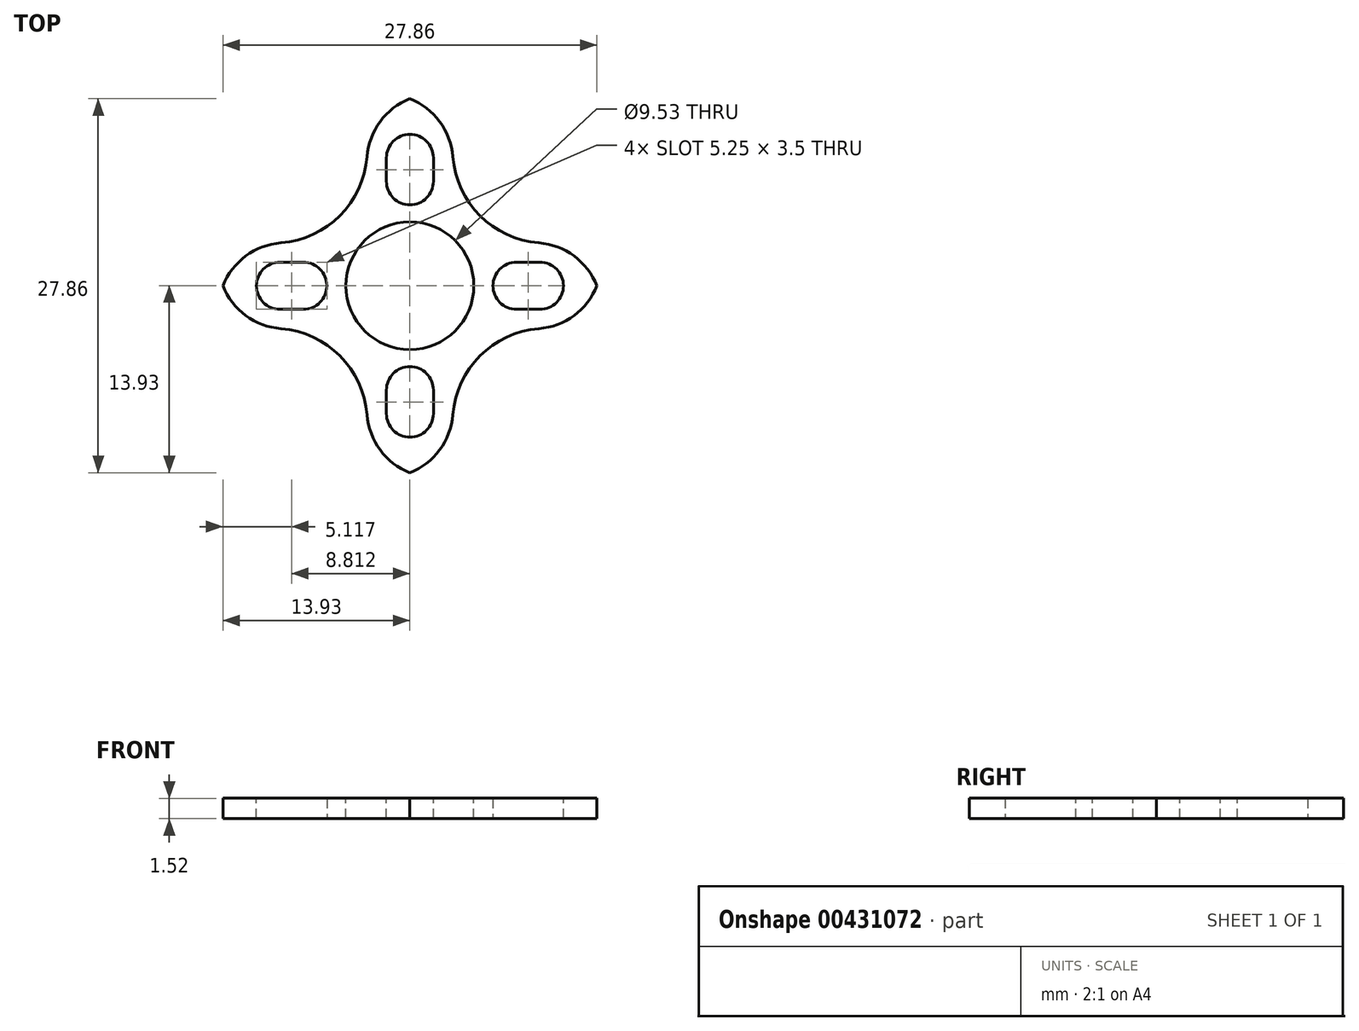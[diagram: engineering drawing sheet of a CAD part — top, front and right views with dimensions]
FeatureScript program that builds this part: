
annotation { "Feature Type Name" : "Feature", "Feature Type Description" : "" }
export const myFeature = defineFeature(function(context is Context, id is Id, definition is map)
    precondition{}
    {
        {
            var Q0;
            Q0=qCreatedBy(makeId("Top.planeOp"),FACE);
            var sketch = newSketch(context, id + "F0", { "sketchPlane" : qUnion([Q0])});
            skCircle(sketch, "E0", {"center": v(0, 9.52) * mm, "radius": 1.75 * mm});
            skCircle(sketch, "E1", {"center": v(0, -9.52) * mm, "radius": 1.75 * mm});
            skCircle(sketch, "E2", {"center": v(-7.94, 0) * mm, "radius": 1.75 * mm});
            skCircle(sketch, "E3", {"center": v(7.94, 0) * mm, "radius": 1.75 * mm});
            skLineSegment(sketch, "E4", {"start": v(-7.94, 0) * mm, "end": v(0, 0) * mm});
            skLineSegment(sketch, "E5", {"start": v(0, 0) * mm, "end": v(7.94, 0) * mm});
            skLineSegment(sketch, "E6", {"start": v(0, 9.53) * mm, "end": v(0, 0) * mm});
            skLineSegment(sketch, "E7", {"start": v(0, -9.53) * mm, "end": v(0, 0) * mm});
            skLineSegment(sketch, "E8", {"start": v(3.18, 14.29) * mm, "end": v(3.18, 3.18) * mm});
            skLineSegment(sketch, "E9", {"start": v(3.17, 3.18) * mm, "end": v(14.29, 3.18) * mm});
            skLineSegment(sketch, "E10", {"start": v(14.29, 3.18) * mm, "end": v(14.29, -3.17) * mm});
            skLineSegment(sketch, "E11", {"start": v(14.29, -3.18) * mm, "end": v(3.17, -3.18) * mm});
            skLineSegment(sketch, "E12", {"start": v(3.18, -3.18) * mm, "end": v(3.18, -14.29) * mm});
            skLineSegment(sketch, "E13", {"start": v(3.17, -14.29) * mm, "end": v(-3.18, -14.29) * mm});
            skLineSegment(sketch, "E14", {"start": v(-3.18, -14.29) * mm, "end": v(-3.18, -3.18) * mm});
            skLineSegment(sketch, "E15", {"start": v(-3.17, -3.18) * mm, "end": v(-14.29, -3.18) * mm});
            skLineSegment(sketch, "E16", {"start": v(-14.29, -3.17) * mm, "end": v(-14.29, 3.18) * mm});
            skLineSegment(sketch, "E17", {"start": v(-14.29, 3.18) * mm, "end": v(-3.18, 3.18) * mm});
            skLineSegment(sketch, "E18", {"start": v(-3.18, 3.18) * mm, "end": v(-3.18, 14.29) * mm});
            skLineSegment(sketch, "E19", {"start": v(-3.18, 14.29) * mm, "end": v(3.17, 14.29) * mm});
            skLineSegment(sketch, "E20", {"start": v(0, -9.52) * mm, "end": v(0, -14.29) * mm, "construction": true});
            skLineSegment(sketch, "E21", {"start": v(7.94, 0) * mm, "end": v(14.29, 0) * mm, "construction": true});
            skSolve(sketch);
        }
        {
            var Q0;
            Q0 = qSketchRegion(id + "F0", true);
            extrude(context, id + "F1", {"entities" : qUnion([Q0]), "depth" : 1.52 * mm});
        }
        {
            var Q0;
            Q0=makeQuery(id+"F1.opExtrude","SWEPT_EDGE",EDGE,{"disambiguationData":[OSD([sQuery(id+"F0.wireOp",EDGE,"E11"),sQuery(id+"F0.wireOp",EDGE,"E12")])]});
            var Q1;
            Q1=makeQuery(id+"F1.opExtrude","SWEPT_EDGE",EDGE,{"disambiguationData":[OSD([sQuery(id+"F0.wireOp",EDGE,"E17"),sQuery(id+"F0.wireOp",EDGE,"E18")])]});
            var Q2;
            Q2=makeQuery(id+"F1.opExtrude","SWEPT_EDGE",EDGE,{"disambiguationData":[OSD([sQuery(id+"F0.wireOp",EDGE,"E8"),sQuery(id+"F0.wireOp",EDGE,"E9")])]});
            var Q3;
            Q3=makeQuery(id+"F1.opExtrude","SWEPT_EDGE",EDGE,{"disambiguationData":[OSD([sQuery(id+"F0.wireOp",EDGE,"E14"),sQuery(id+"F0.wireOp",EDGE,"E15")])]});
            fillet(context, id + "F2", {"entities" : qUnion([Q0, Q1, Q2, Q3]), "radius" : 7 * mm, "tangentPropagation" : true, "allowEdgeOverflow" : false});
        }
        {
            var Q0;
            Q0=makeQuery(id+"F1.opExtrude","SWEPT_EDGE",EDGE,{"disambiguationData":[OSD([sQuery(id+"F0.wireOp",EDGE,"E8"),sQuery(id+"F0.wireOp",EDGE,"E19")])]});
            var Q1;
            Q1=makeQuery(id+"F1.opExtrude","SWEPT_EDGE",EDGE,{"disambiguationData":[OSD([sQuery(id+"F0.wireOp",EDGE,"E18"),sQuery(id+"F0.wireOp",EDGE,"E19")])]});
            var Q2;
            Q2=makeQuery(id+"F1.opExtrude","SWEPT_EDGE",EDGE,{"disambiguationData":[OSD([sQuery(id+"F0.wireOp",EDGE,"E15"),sQuery(id+"F0.wireOp",EDGE,"E16")])]});
            var Q3;
            Q3=makeQuery(id+"F1.opExtrude","SWEPT_EDGE",EDGE,{"disambiguationData":[OSD([sQuery(id+"F0.wireOp",EDGE,"E16"),sQuery(id+"F0.wireOp",EDGE,"E17")])]});
            var Q4;
            Q4=makeQuery(id+"F1.opExtrude","SWEPT_EDGE",EDGE,{"disambiguationData":[OSD([sQuery(id+"F0.wireOp",EDGE,"E13"),sQuery(id+"F0.wireOp",EDGE,"E14")])]});
            var Q5;
            Q5=makeQuery(id+"F1.opExtrude","SWEPT_EDGE",EDGE,{"disambiguationData":[OSD([sQuery(id+"F0.wireOp",EDGE,"E12"),sQuery(id+"F0.wireOp",EDGE,"E13")])]});
            var Q6;
            Q6=makeQuery(id+"F1.opExtrude","SWEPT_EDGE",EDGE,{"disambiguationData":[OSD([sQuery(id+"F0.wireOp",EDGE,"E10"),sQuery(id+"F0.wireOp",EDGE,"E11")])]});
            var Q7;
            Q7=makeQuery(id+"F1.opExtrude","SWEPT_EDGE",EDGE,{"disambiguationData":[OSD([sQuery(id+"F0.wireOp",EDGE,"E9"),sQuery(id+"F0.wireOp",EDGE,"E10")])]});
            fillet(context, id + "F3", {"entities" : qUnion([Q0, Q1, Q2, Q3, Q4, Q5, Q6, Q7]), "radius" : 5.08 * mm, "tangentPropagation" : true, "allowEdgeOverflow" : false});
        }
        {
            var Q0;
            Q0=makeQuery(id+"F1.opExtrude","CAP_FACE",FACE,{"disambiguationData":[OSD([sQuery(id+"F0.wireOp",EDGE,"E0"),sQuery(id+"F0.wireOp",EDGE,"E1"),sQuery(id+"F0.wireOp",EDGE,"E2"),sQuery(id+"F0.wireOp",EDGE,"E3"),sQuery(id+"F0.wireOp",EDGE,"E8"),sQuery(id+"F0.wireOp",EDGE,"E9"),sQuery(id+"F0.wireOp",EDGE,"E10"),sQuery(id+"F0.wireOp",EDGE,"E11"),sQuery(id+"F0.wireOp",EDGE,"E12"),sQuery(id+"F0.wireOp",EDGE,"E13"),sQuery(id+"F0.wireOp",EDGE,"E14"),sQuery(id+"F0.wireOp",EDGE,"E15"),sQuery(id+"F0.wireOp",EDGE,"E16"),sQuery(id+"F0.wireOp",EDGE,"E17"),sQuery(id+"F0.wireOp",EDGE,"E18"),sQuery(id+"F0.wireOp",EDGE,"E19")])],"isStart":false});
            var sketch = newSketch(context, id + "F4", { "sketchPlane" : qUnion([Q0])});
            skCircle(sketch, "E22", {"center": v(0, 0) * mm, "radius": 4.76 * mm});
            skLineSegment(sketch, "E23", {"start": v(-7.94, 0) * mm, "end": v(-9.69, 0) * mm});
            skLineSegment(sketch, "E24", {"start": v(0, 9.52) * mm, "end": v(0, 7.77) * mm});
            skLineSegment(sketch, "E25", {"start": v(7.94, 0) * mm, "end": v(9.69, 0) * mm});
            skLineSegment(sketch, "E26", {"start": v(0, -9.52) * mm, "end": v(0, -7.77) * mm});
            skArc(sketch, "E27.0.startCap", {"start": v(-1.75, 9.52) * mm, "mid": v(0, 11.27) * mm, "end": v(1.75, 9.52) * mm});
            skArc(sketch, "E27.0.endCap", {"start": v(1.75, 7.77) * mm, "mid": v(0, 6.02) * mm, "end": v(-1.75, 7.77) * mm});
            skLineSegment(sketch, "E27.0.left", {"start": v(1.75, 9.52) * mm, "end": v(1.75, 7.77) * mm});
            skLineSegment(sketch, "E27.0.right", {"start": v(-1.75, 9.52) * mm, "end": v(-1.75, 7.77) * mm});
            skArc(sketch, "E28.0.startCap", {"start": v(1.75, -9.52) * mm, "mid": v(0, -11.27) * mm, "end": v(-1.75, -9.52) * mm});
            skArc(sketch, "E28.0.endCap", {"start": v(-1.75, -7.77) * mm, "mid": v(0, -6.02) * mm, "end": v(1.75, -7.77) * mm});
            skLineSegment(sketch, "E28.0.left", {"start": v(-1.75, -9.52) * mm, "end": v(-1.75, -7.77) * mm});
            skLineSegment(sketch, "E28.0.right", {"start": v(1.75, -9.52) * mm, "end": v(1.75, -7.77) * mm});
            skArc(sketch, "E29.0.startCap", {"start": v(7.94, -1.75) * mm, "mid": v(6.19, 0) * mm, "end": v(7.94, 1.75) * mm});
            skArc(sketch, "E29.0.endCap", {"start": v(9.69, 1.75) * mm, "mid": v(11.44, 0) * mm, "end": v(9.69, -1.75) * mm});
            skLineSegment(sketch, "E29.0.left", {"start": v(7.94, 1.75) * mm, "end": v(9.69, 1.75) * mm});
            skLineSegment(sketch, "E29.0.right", {"start": v(7.94, -1.75) * mm, "end": v(9.69, -1.75) * mm});
            skArc(sketch, "E30.0.startCap", {"start": v(-7.94, 1.75) * mm, "mid": v(-6.19, 0) * mm, "end": v(-7.94, -1.75) * mm});
            skArc(sketch, "E30.0.endCap", {"start": v(-9.69, -1.75) * mm, "mid": v(-11.44, 0) * mm, "end": v(-9.69, 1.75) * mm});
            skLineSegment(sketch, "E30.0.left", {"start": v(-7.94, -1.75) * mm, "end": v(-9.69, -1.75) * mm});
            skLineSegment(sketch, "E30.0.right", {"start": v(-7.94, 1.75) * mm, "end": v(-9.69, 1.75) * mm});
            skSolve(sketch);
        }
        {
            var Q0;
            Q0 = qSketchRegion(id + "F4", true);
            extrude(context, id + "F5", {"entities" : qUnion([Q0]), "operationType" : NewBodyOperationType.REMOVE, "oppositeDirection" : true, "depth" : 25.4 * mm});
        }
    });
